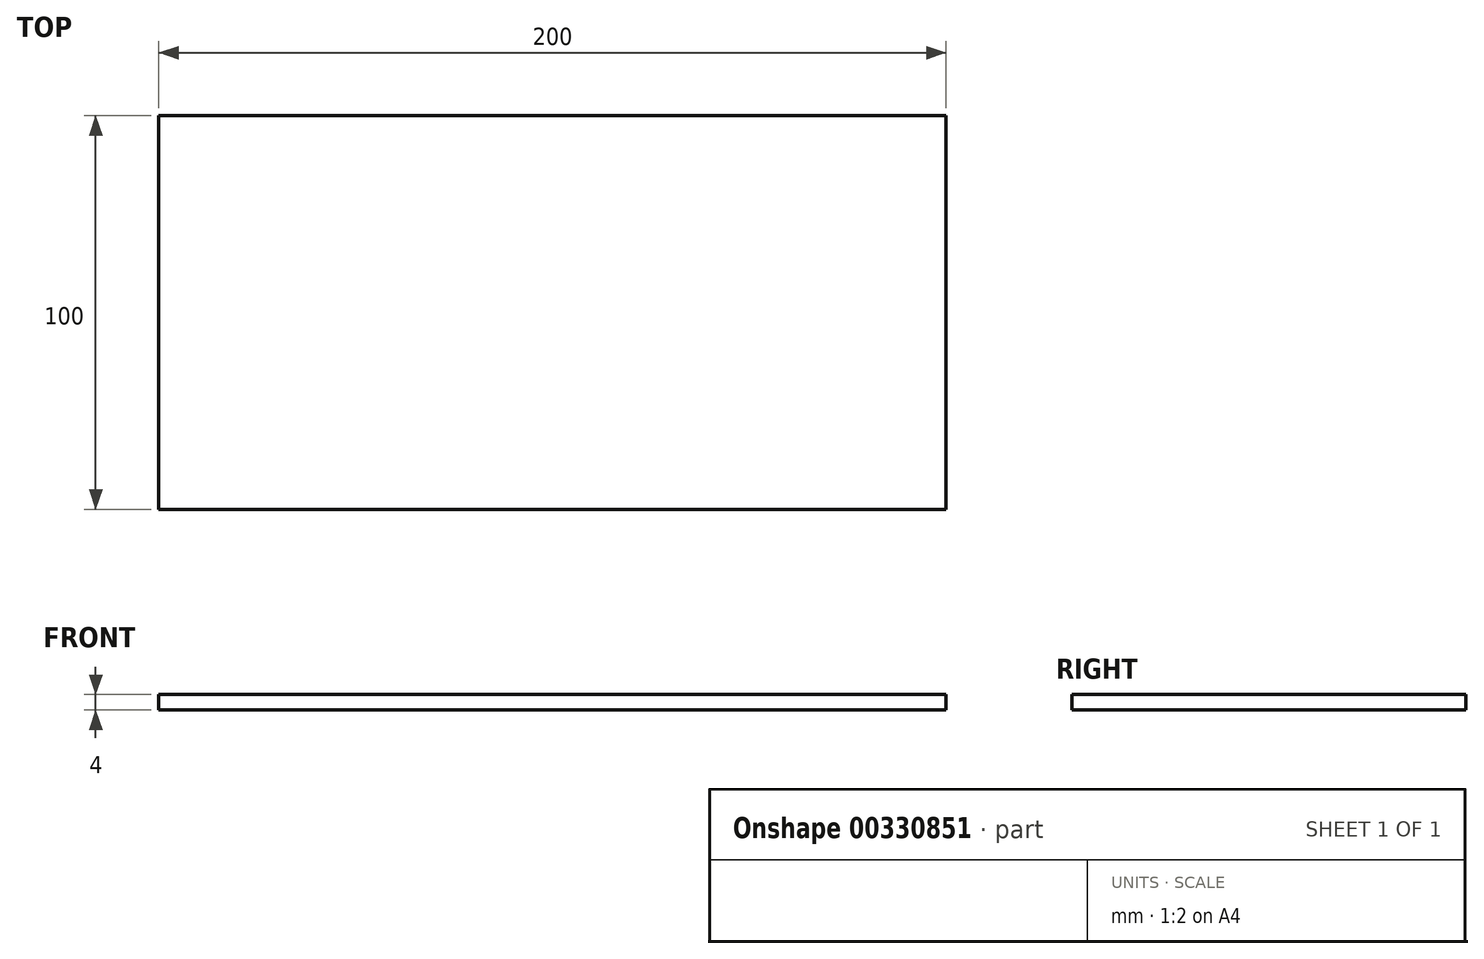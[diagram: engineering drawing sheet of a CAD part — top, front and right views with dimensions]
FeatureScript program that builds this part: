
annotation { "Feature Type Name" : "Feature", "Feature Type Description" : "" }
export const myFeature = defineFeature(function(context is Context, id is Id, definition is map)
    precondition{}
    {
        {
            var Q0;
            Q0=qCreatedBy(makeId("Top.planeOp"),FACE);
            var sketch = newSketch(context, id + "F0", { "sketchPlane" : qUnion([Q0])});
            skLineSegment(sketch, "E0.bottom", {"start": v(-152.64, 75.46) * mm, "end": v(47.36, 75.46) * mm});
            skLineSegment(sketch, "E0.top", {"start": v(-152.64, -24.54) * mm, "end": v(47.36, -24.54) * mm});
            skLineSegment(sketch, "E0.left", {"start": v(-152.64, 75.46) * mm, "end": v(-152.64, -24.54) * mm});
            skLineSegment(sketch, "E0.right", {"start": v(47.36, 75.46) * mm, "end": v(47.36, -24.54) * mm});
            skSolve(sketch);
        }
        {
            var Q0;
            Q0=makeQuery(id+"F0.imprint","IMPRINT",FACE,{"disambiguationData":[TD([[makeQuery(id+"F0.imprint","IMPRINT",EDGE,{"derivedFrom":sQuery(id+"F0.wireOp",EDGE,"E0.bottom")}),-1.0]])]});
            extrude(context, id + "F1", {"entities" : qUnion([Q0]), "depth" : 4 * mm});
        }
    });
